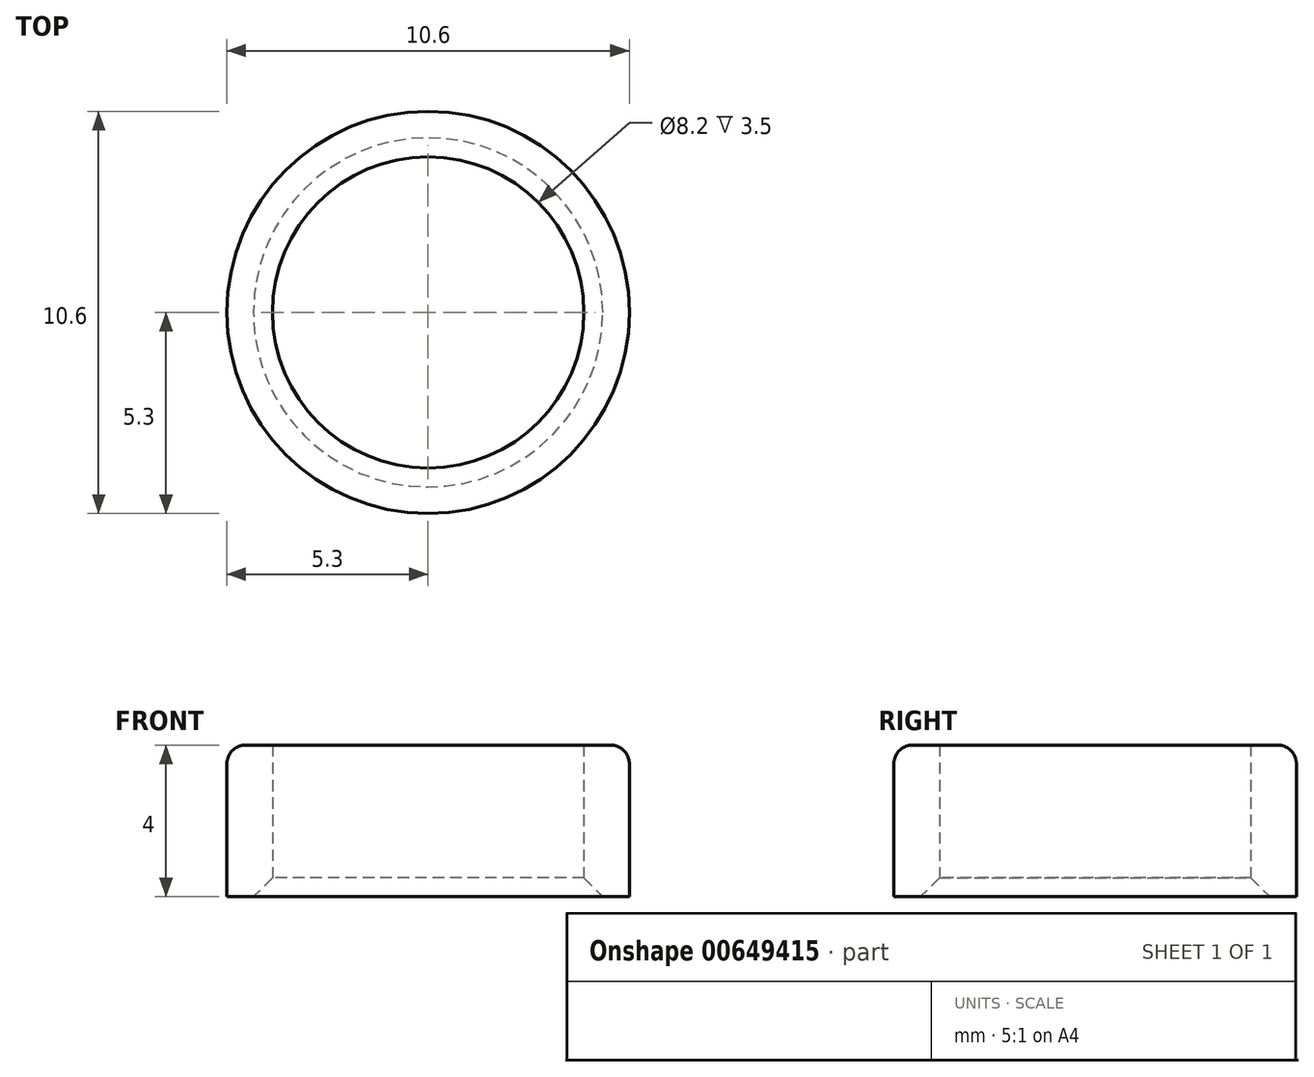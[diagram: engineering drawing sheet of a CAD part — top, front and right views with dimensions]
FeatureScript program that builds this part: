
annotation { "Feature Type Name" : "Feature", "Feature Type Description" : "" }
export const myFeature = defineFeature(function(context is Context, id is Id, definition is map)
    precondition{}
    {
        {
            var Q0;
            Q0=qCreatedBy(makeId("Top.planeOp"),FACE);
            var sketch = newSketch(context, id + "F0", { "sketchPlane" : qUnion([Q0])});
            skCircle(sketch, "E0", {"center": v(0, 0) * mm, "radius": 4.1 * mm});
            skCircle(sketch, "E1", {"center": v(0, 0) * mm, "radius": 5.3 * mm});
            skSolve(sketch);
        }
        {
            var Q0;
            Q0 = qSketchRegion(id + "F0", true);
            extrude(context, id + "F1", {"entities" : qUnion([Q0]), "depth" : 4 * mm, "offsetDistance" : 25.4 * mm});
        }
        {
            var Q0;
            Q0=makeQuery(id+"F1.opExtrude","CAP_EDGE",EDGE,{"disambiguationData":[OSD([sQuery(id+"F0.wireOp",EDGE,"E0")])],"isStart":true});
            chamfer(context, id + "F2", {"entities" : qUnion([Q0]), "width" : .5 * mm, "tangentPropagation" : true});
        }
        {
            var Q0;
            Q0=makeQuery(id+"F1.opExtrude","CAP_EDGE",EDGE,{"disambiguationData":[OSD([sQuery(id+"F0.wireOp",EDGE,"E1")])],"isStart":false});
            fillet(context, id + "F3", {"entities" : qUnion([Q0]), "radius" : .5 * mm, "tangentPropagation" : true, "allowEdgeOverflow" : false});
        }
    });
